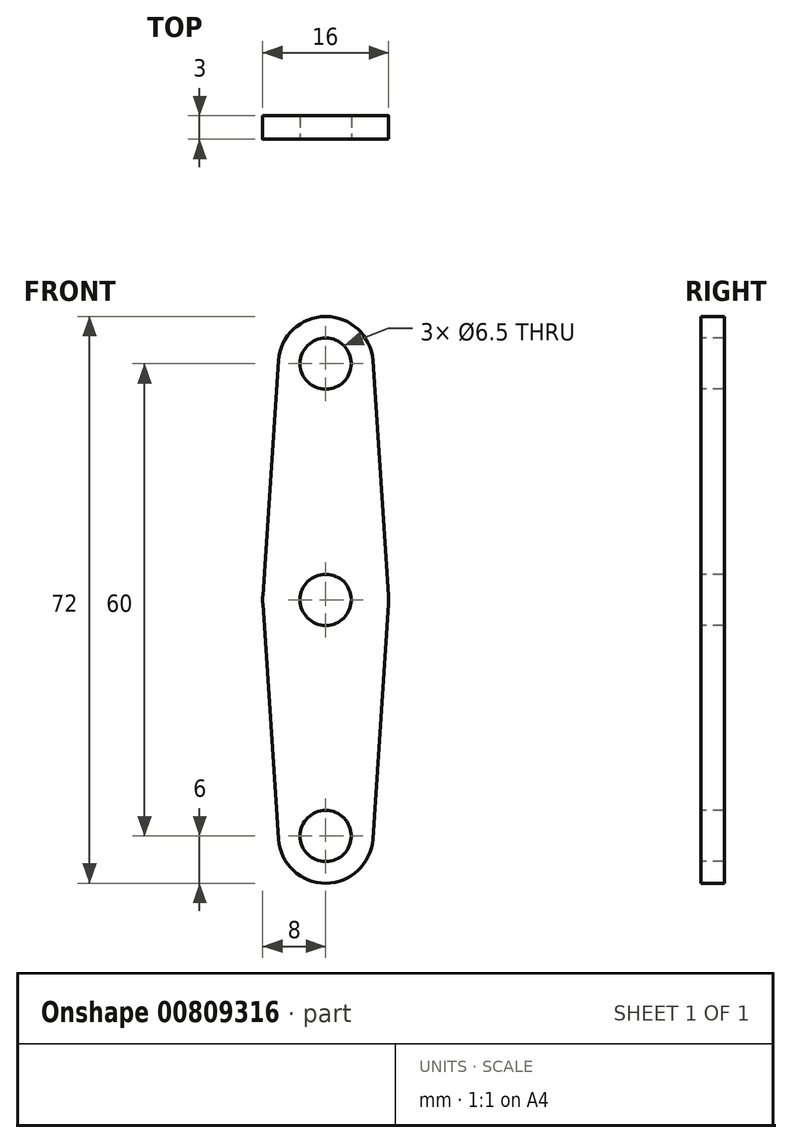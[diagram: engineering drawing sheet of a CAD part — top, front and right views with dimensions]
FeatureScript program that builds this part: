
annotation { "Feature Type Name" : "Feature", "Feature Type Description" : "" }
export const myFeature = defineFeature(function(context is Context, id is Id, definition is map)
    precondition{}
    {
        {
            assignVariable(context, id + "F0", {"name" : "NoCarrier", "anyValue" : 2});
        }
        {
            assignVariable(context, id + "F1", {"name" : "Thickness", "anyValue" : 3 * mm});
        }
        {
            var Q0;
            Q0=qCreatedBy(makeId("Front.planeOp"),FACE);
            var sketch = newSketch(context, id + "F2", { "sketchPlane" : qUnion([Q0])});
            skArc(sketch, "E0", {"start": v(-7.98, 0.53) * mm, "mid": v(0, -8) * mm, "end": v(7.98, 0.53) * mm});
            skArc(sketch, "E1", {"start": v(5.99, 30.4) * mm, "mid": v(0, 36) * mm, "end": v(-5.99, 30.4) * mm});
            skLineSegment(sketch, "E2", {"start": v(-5.99, 30.4) * mm, "end": v(-7.98, 0.53) * mm});
            skLineSegment(sketch, "E3", {"start": v(5.99, 30.4) * mm, "end": v(7.98, 0.53) * mm});
            skSolve(sketch);
        }
        {
            var Q0;
            Q0 = qSketchRegion(id + "F2", true);
            extrude(context, id + "F3", {"entities" : qUnion([Q0]), "endBound" : BoundingType.SYMMETRIC, "depth" : getVariable(context, 'Thickness'), "offsetDistance" : 25 * mm});
        }
        {
            var Q0;
            Q0=makeQuery(id+"F3.opExtrude","CAP_FACE",FACE,{"disambiguationData":[OSD([sQuery(id+"F2.wireOp",EDGE,"E0"),sQuery(id+"F2.wireOp",EDGE,"E1"),sQuery(id+"F2.wireOp",EDGE,"E2"),sQuery(id+"F2.wireOp",EDGE,"E3")])],"isStart":false});
            var sketch = newSketch(context, id + "F4", { "sketchPlane" : qUnion([Q0])});
            skCircle(sketch, "E4", {"center": v(0, 30) * mm, "radius": 3.25 * mm});
            skSolve(sketch);
        }
        {
            var Q0;
            Q0=makeQuery(id+"F4.imprint","IMPRINT",FACE,{"disambiguationData":[TD([[makeQuery(id+"F4.imprint","IMPRINT",EDGE,{"derivedFrom":sQuery(id+"F4.wireOp",EDGE,"E4")}),1.0]])]});
            extrude(context, id + "F5", {"entities" : qUnion([Q0]), "operationType" : NewBodyOperationType.REMOVE, "endBound" : BoundingType.UP_TO_NEXT, "oppositeDirection" : true, "depth" : 25 * mm, "offsetDistance" : 25 * mm});
        }
        {
            var Q0;
            Q0=makeQuery(id+"F3.opExtrude","SWEPT_BODY",BODY,{"disambiguationData":[OSD([sQuery(id+"F2.wireOp",EDGE,"E0"),sQuery(id+"F2.wireOp",EDGE,"E1"),sQuery(id+"F2.wireOp",EDGE,"E2"),sQuery(id+"F2.wireOp",EDGE,"E3")])]});
            var Q1;
            Q1=makeQuery(id+"F3.opExtrude","SWEPT_FACE",FACE,{"disambiguationData":[OSD([sQuery(id+"F2.wireOp",EDGE,"E0")])]});
            circularPattern(context, id + "F6", {"operationType" : NewBodyOperationType.ADD, "entities" : qUnion([Q0]), "axis" : qUnion([Q1]), "angle" : 360 * degree, "instanceCount" : getVariable(context, 'NoCarrier'), "equalSpace" : true});
        }
        {
            var Q0;
            {var subQ0=makeQuery(id+"F3.opExtrude","CAP_FACE",FACE,{"disambiguationData":[OSD([sQuery(id+"F2.wireOp",EDGE,"E0"),sQuery(id+"F2.wireOp",EDGE,"E1"),sQuery(id+"F2.wireOp",EDGE,"E2"),sQuery(id+"F2.wireOp",EDGE,"E3")])],"isStart":false});Q0=makeQuery(id+"F6.boolean.opBoolean","MERGE",FACE,{"derivedFrom":[subQ0,makeQuery(id+"F6.opPattern","COPY",FACE,{"derivedFrom":subQ0,"instanceName":"1"})]});}
            var sketch = newSketch(context, id + "F7", { "sketchPlane" : qUnion([Q0])});
            skCircle(sketch, "E5", {"center": v(0, 0) * mm, "radius": 3.25 * mm});
            skSolve(sketch);
        }
        {
            var Q0;
            Q0=makeQuery(id+"F7.imprint","IMPRINT",FACE,{"disambiguationData":[TD([[makeQuery(id+"F7.imprint","IMPRINT",EDGE,{"derivedFrom":sQuery(id+"F7.wireOp",EDGE,"E5")}),1.0]])]});
            extrude(context, id + "F8", {"entities" : qUnion([Q0]), "operationType" : NewBodyOperationType.REMOVE, "oppositeDirection" : true, "depth" : 25 * mm, "offsetDistance" : 25 * mm});
        }
    });
